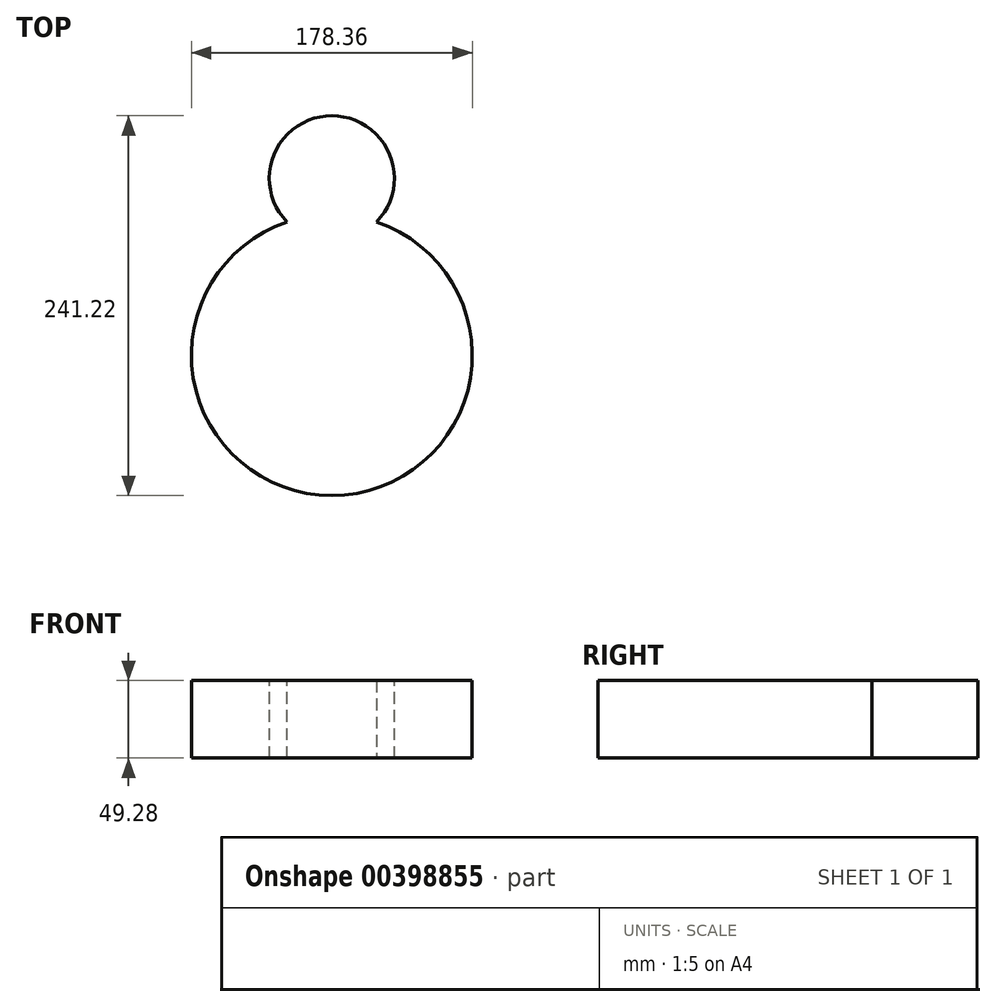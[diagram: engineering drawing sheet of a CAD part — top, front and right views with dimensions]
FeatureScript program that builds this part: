
annotation { "Feature Type Name" : "Feature", "Feature Type Description" : "" }
export const myFeature = defineFeature(function(context is Context, id is Id, definition is map)
    precondition{}
    {
        {
            var Q0;
            Q0=qCreatedBy(makeId("Top.planeOp"),FACE);
            var sketch = newSketch(context, id + "F0", { "sketchPlane" : qUnion([Q0])});
            skLineSegment(sketch, "E0", {"start": v(0, 55.57) * mm, "end": v(0, -56.76) * mm});
            skLineSegment(sketch, "E1", {"start": v(0, -56.76) * mm, "end": v(28.38, 27.79) * mm});
            skLineSegment(sketch, "E2", {"start": v(28.38, 27.79) * mm, "end": v(0, 55.57) * mm});
            skSolve(sketch);
        }
        {
            var Q0;
            Q0=makeQuery(id+"F0.imprint","IMPRINT",FACE,{"disambiguationData":[TD([[makeQuery(id+"F0.imprint","IMPRINT",EDGE,{"derivedFrom":sQuery(id+"F0.wireOp",EDGE,"E0")}),1.0]])]});
            extrude(context, id + "F1", {"entities" : qUnion([Q0]), "depth" : 49.28 * mm});
        }
        {
            var Q0;
            Q0=makeQuery(id+"F1.opExtrude","SWEPT_FACE",FACE,{"disambiguationData":[OSD([sQuery(id+"F0.wireOp",EDGE,"E2")])]});
            var Q1;
            Q1=makeQuery(id+"F1.opExtrude","SWEPT_EDGE",EDGE,{"disambiguationData":[OSD([sQuery(id+"F0.wireOp",EDGE,"E0"),sQuery(id+"F0.wireOp",EDGE,"E2")])]});
            revolve(context, id + "F2", {"operationType" : NewBodyOperationType.ADD, "entities" : qUnion([Q0]), "axis" : qUnion([Q1]), "revolveType" : RevolveType.FULL});
        }
        {
            var Q0;
            Q0=makeQuery(id+"F1.opExtrude","SWEPT_FACE",FACE,{"disambiguationData":[OSD([sQuery(id+"F0.wireOp",EDGE,"E1")])]});
            var Q1;
            Q1=makeQuery(id+"F1.opExtrude","SWEPT_EDGE",EDGE,{"disambiguationData":[OSD([sQuery(id+"F0.wireOp",EDGE,"E0"),sQuery(id+"F0.wireOp",EDGE,"E1")])]});
            revolve(context, id + "F3", {"operationType" : NewBodyOperationType.ADD, "entities" : qUnion([Q0]), "axis" : qUnion([Q1]), "revolveType" : RevolveType.FULL});
        }
    });
